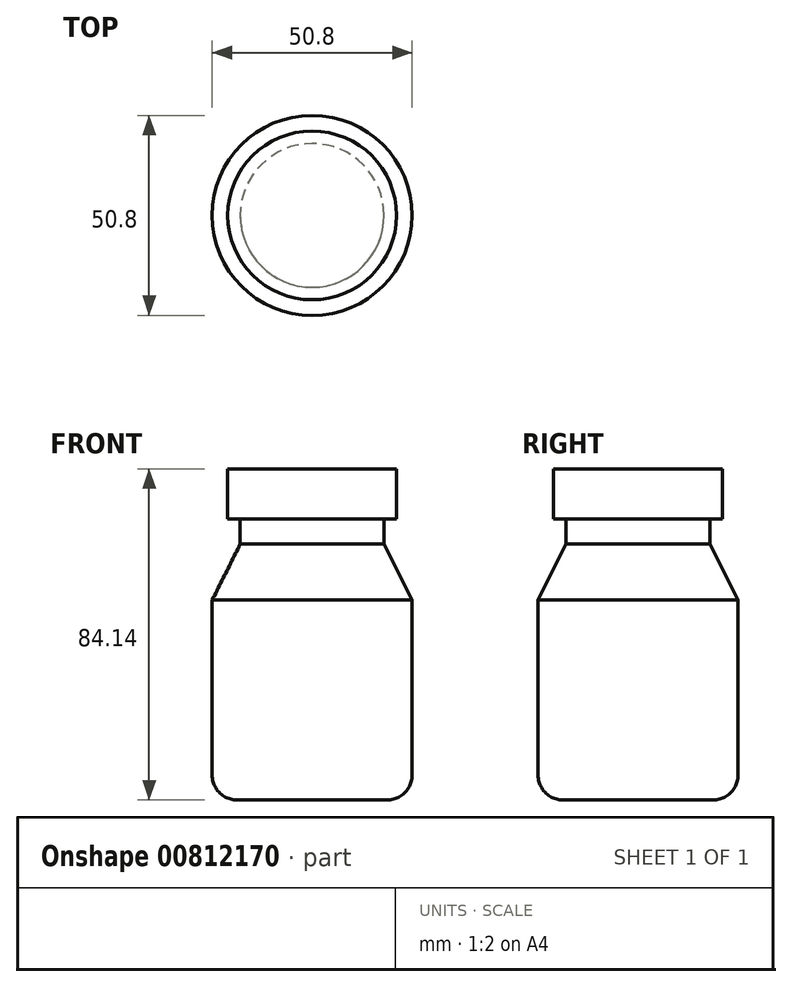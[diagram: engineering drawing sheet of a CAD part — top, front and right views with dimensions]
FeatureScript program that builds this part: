
annotation { "Feature Type Name" : "Feature", "Feature Type Description" : "" }
export const myFeature = defineFeature(function(context is Context, id is Id, definition is map)
    precondition{}
    {
        {
            var Q0;
            Q0=qCreatedBy(makeId("Top.planeOp"),FACE);
            var sketch = newSketch(context, id + "F0", { "sketchPlane" : qUnion([Q0])});
            skCircle(sketch, "E0", {"center": v(0, 0) * mm, "radius": 25.4 * mm});
            skCircle(sketch, "E1", {"center": v(0, 0) * mm, "radius": 21.43 * mm});
            skCircle(sketch, "E2", {"center": v(0, 0) * mm, "radius": 18.26 * mm});
            skSolve(sketch);
        }
        {
            var Q0;
            Q0=makeQuery(id+"F0.imprint","IMPRINT",FACE,{"disambiguationData":[TD([[makeQuery(id+"F0.imprint","IMPRINT",EDGE,{"derivedFrom":sQuery(id+"F0.wireOp",EDGE,"E0")}),1.0]])]});
            var Q1;
            Q1=makeQuery(id+"F0.imprint","IMPRINT",FACE,{"disambiguationData":[TD([[makeQuery(id+"F0.imprint","IMPRINT",EDGE,{"derivedFrom":sQuery(id+"F0.wireOp",EDGE,"E1")}),1.0]])]});
            extrude(context, id + "F1", {"entities" : qUnion([Q0, Q1]), "depth" : 66.67 * mm, "offsetDistance" : 25.4 * mm});
        }
        {
            var Q0;
            Q0=makeQuery(id+"F0.imprint","IMPRINT",FACE,{"disambiguationData":[TD([[makeQuery(id+"F0.imprint","IMPRINT",EDGE,{"derivedFrom":sQuery(id+"F0.wireOp",EDGE,"E2")}),1.0]])]});
            extrude(context, id + "F2", {"entities" : qUnion([Q0]), "operationType" : NewBodyOperationType.ADD, "depth" : 84.14 * mm, "offsetDistance" : 25.4 * mm});
        }
        {
            var Q0;
            Q0=makeQuery(id+"F1.opExtrude","CAP_EDGE",EDGE,{"disambiguationData":[OSD([sQuery(id+"F0.wireOp",EDGE,"E0")])],"isStart":true});
            fillet(context, id + "F3", {"entities" : qUnion([Q0]), "radius" : 6.35 * mm, "tangentPropagation" : true, "allowEdgeOverflow" : false});
        }
        {
            var Q0;
            Q0=makeQuery(id+"F1.opExtrude","CAP_EDGE",EDGE,{"disambiguationData":[OSD([sQuery(id+"F0.wireOp",EDGE,"E0")])],"isStart":false});
            chamfer(context, id + "F4", {"entities" : qUnion([Q0]), "chamferType" : ChamferType.TWO_OFFSETS, "width1" : 7.94 * mm, "oppositeDirection" : false, "width2" : 15.88 * mm, "tangentPropagation" : true});
        }
        {
            var Q0;
            Q0=makeQuery(id+"F0.imprint","IMPRINT",FACE,{"disambiguationData":[TD([[makeQuery(id+"F0.imprint","IMPRINT",EDGE,{"derivedFrom":sQuery(id+"F0.wireOp",EDGE,"E1")}),1.0]])]});
            extrude(context, id + "F5", {"entities" : qUnion([Q0]), "operationType" : NewBodyOperationType.ADD, "depth" : 84.14 * mm, "offsetDistance" : 25.4 * mm, "hasSecondDirection" : true, "secondDirectionOppositeDirection" : false, "secondDirectionDepth" : 71.44 * mm});
        }
    });
